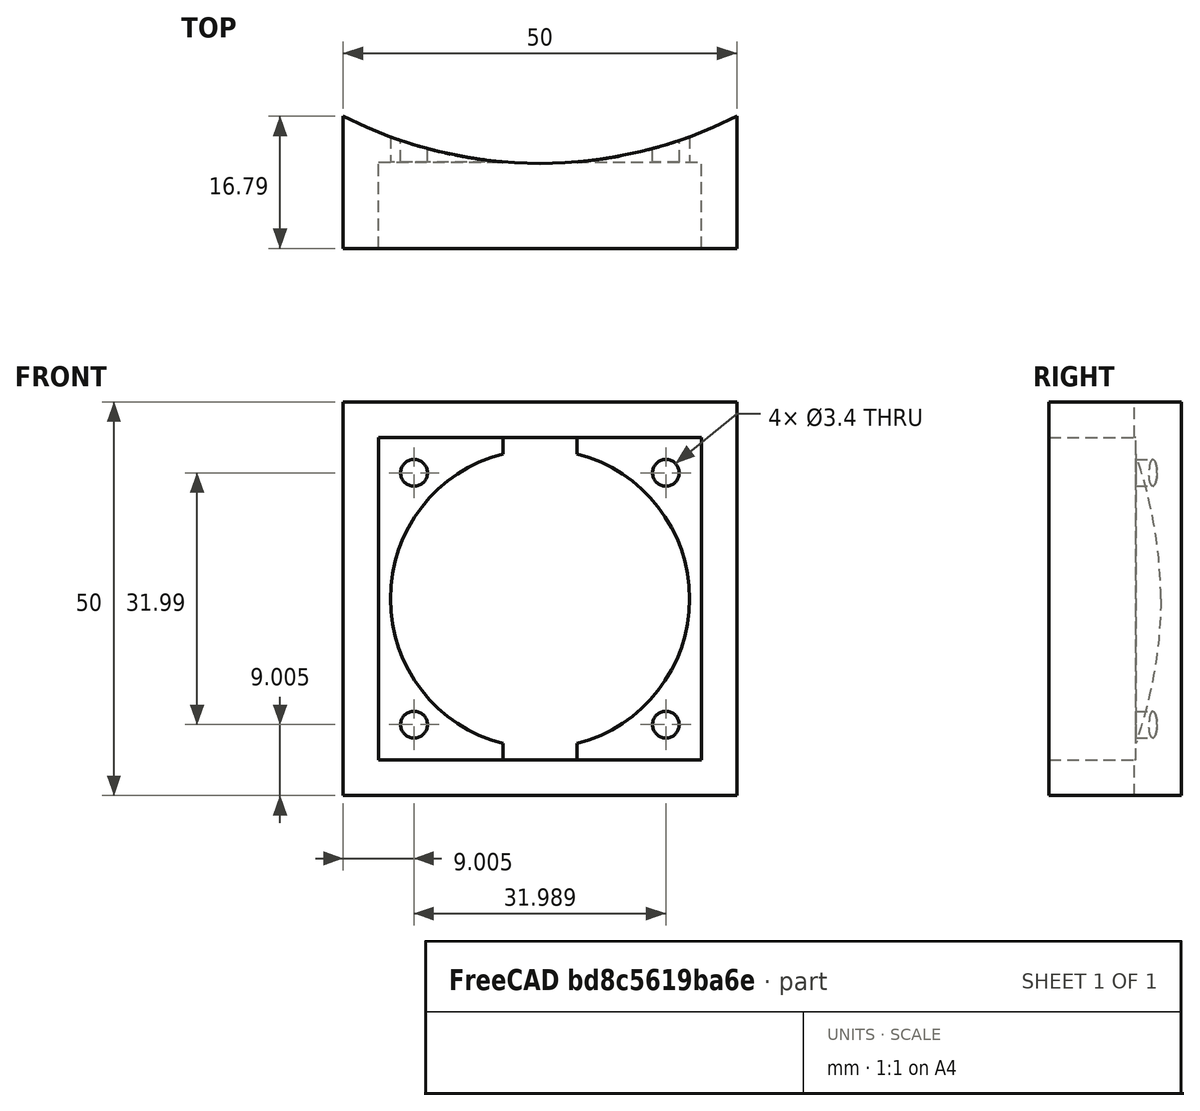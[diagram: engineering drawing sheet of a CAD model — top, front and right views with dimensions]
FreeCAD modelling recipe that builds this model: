
FCSTD DOCUMENT  (FreeCAD 0.16R6703 (Git))
Label: Art4BodyFan2
License: All rights reserved
LicenseURL: http://en.wikipedia.org/wiki/All_rights_reserved
objects: Part::Cylinder×4, Part::Cut×4, Part::FeaturePython×4, Part::MultiFuse×2, Part::Box×2, App::DocumentObjectGroup×1
note: 16 computed .brp shape members not serialized (recipe doc carries the construction recipe); baked Part::Feature solids carry a one-line shape summary decoded from their .brp

FEATURE [Part::Cylinder] Cylinder  label="M3BoltHead"
  Angle = 360
  Height = 7
  Radius = 2.95
FEATURE [Part::Cylinder] Cylinder001  label="M3BoltBody"
  Angle = 360
  Height = 30
  Placement = pos=(0,0,6) rot=(0,0,1;0rad)
  Radius = 1.7
FEATURE [Part::MultiFuse] Fusion  label="M3Bolt"
  Shapes = -> [Cylinder001,Cylinder]
FEATURE [App::DocumentObjectGroup] Group  label="Master"
  Group = -> [Fusion]
FEATURE [Part::Box] Box  label="Cube"
  Height = 50
  Length = 50
  Placement = pos=(-25,-66,0) rot=(0,0,1;0rad)
  Width = 25
FEATURE [Part::Cylinder] Cylinder1063  label="Cylinder"
  Angle = 360
  Height = 50
  Radius = 55.2
FEATURE [Part::Cut] Cut
  Base = -> Box
  Tool = -> Cylinder1063
FEATURE [Part::Cylinder] Cylinder1064  label="Cylinder022"
  Angle = 360
  Height = 20
  Placement = pos=(3.51623e-05,-47,25) rot=(1,0,0;1.5708rad)
  Radius = 19
FEATURE [Part::Cut] Cut149
  Base = -> Cut
  Tool = -> Cylinder1064
FEATURE [Part::Box] Box272  label="Cube034"
  Height = 41
  Length = 41
  Placement = pos=(-20.5,-66,4.5) rot=(0,0,1;0rad)
  Width = 11
FEATURE [Part::Cut] Cut150
  Base = -> Cut149
  Tool = -> Box272
FEATURE [Part::FeaturePython] Clone  label="Clone of M3Bolt"  # Draft clone (typed FeaturePython)
  Objects = -> [Fusion]
  Placement = pos=(15.9948,-81.76,9.00524) rot=(-1,0,0;1.5708rad)
  Scale = (1,1,1)
FEATURE [Part::FeaturePython] Clone001  label="Clone of M3Bolt001"  # Draft clone (typed FeaturePython)
  Objects = -> [Fusion]
  Placement = pos=(-15.9947,-81.76,9.00524) rot=(-1,0,0;1.5708rad)
  Scale = (1,1,1)
FEATURE [Part::FeaturePython] Clone002  label="Clone of M3Bolt002"  # Draft clone (typed FeaturePython)
  Objects = -> [Fusion]
  Placement = pos=(15.9948,-81.76,40.9948) rot=(-1,0,0;1.5708rad)
  Scale = (1,1,1)
FEATURE [Part::FeaturePython] Clone003  label="Clone of M3Bolt003"  # Draft clone (typed FeaturePython)
  Objects = -> [Fusion]
  Placement = pos=(-15.9947,-81.76,40.9948) rot=(-1,0,0;1.5708rad)
  Scale = (1,1,1)
FEATURE [Part::MultiFuse] Fusion001
  Shapes = -> [Clone,Clone003,Clone001,Clone002]
FEATURE [Part::Cut] Cut151  label="Art4BodyFan"
  Base = -> Cut150
  Tool = -> Fusion001
